# Revit family: IS_Calla_E2518_BIM_GB
name_source: partatom
category: Plumbing Fixtures
units: mm (PartAtom-declared; Revit-internal decimal feet)

## family parameters
Always vertical = No
Cut with Voids When Loaded = No
OmniClass Number = 23.45.05.21.11.11
OmniClass Title = Water Operated Water Closets
Part Type = Normal
Room Calculation Point = No
Round Connector Dimension = Use Diameter
Shared = No
Work Plane-Based = No

## types (2) — shared parameters
AreaUnits = Millimeters
BIMObjectName = IS_IdealStandard_WCseatsandcovers_Calla_E2518
BIMobject category = Wash Basins
BIMobject category code = wash-basins
BIMobject main category = Sanitary
BIMobject main category code = sanitary
BarCode = 5017830556480
Brand = Ideal Standard
Brand url = http://www.idealstandard.co.uk
Color = Gloss White
ConnectionType = Plumbing
CurrencyUnit = £
CurrentRevision = 1
Date of publishing = 15/12/2021
DurationUnit = Years
Edition number = 1
ExpectedLife = 5
Finish = Gloss White
GTIN code = https://5017830556480
Help = https://www.idealstandard.co.uk
IFC Classification = Sanitary Terminal
IfcExportAs = IfcSanitaryTerminalType
IfcExportType = WCSEAT
Installation instructions = https://www.idealstandard.co.uk
InstallationInstructions = https://www.idealstandard.co.uk
LinearUnits = Millimeter
MainColor = Gloss White
MaintenanceInformation = https://www.idealstandard.co.uk
Manufacturer = Ideal Standard
Manufacturer name = Ideal Standard
ManufacturerURL = https://www.idealstandard.co.uk
Material = MDF
Material main = MDF
NBS Reference Code = 45-35-70/391
NBS Reference Description = WC seats and covers
Name = WCseatsandcovers_Calla_E2518_IdealStandard
NettWeight = 3.4
NominalDepth = 432 mm
NominalHeight = 59 mm
NominalLength = 432 mm
NominalWidth = 363 mm
OmniClass Code = 23-31 19 00
OmniClass Description = Toilets
Product Guid = 6a91e68a-2435-4611-9eab-a73c43033e42
Product SKU = E2518
Product certification = https://www.idealstandard.co.uk
Product data url = https://bimobject.com
Product family = Calla
Product group = WC Seats
Product name = Calla Sandwich Seat & Cover Soft Closure
Product url = https://www.idealstandard.co.uk
ProductInformation = https://www.idealstandard.co.uk
QR code = http://bimobject.com
Shape = sculptured
Size = 363 x 432 x 59 mm
Space = Internal
SpareParts = https://fastpart-spares.co.uk
Technical description = https://www.idealstandard.co.uk
UNSPSC Code = 30181511
URL = https://www.idealstandard.co.uk
Uniclass 1.4 Code = L72163
Uniclass 1.4 Description = Pans, seats
Uniclass 2.0 Code = PR-31-79
Uniclass 2.0 Description = Sink, Wash Basins And Troughs
Uniclass 2015 Code = Pr_40_20_93_95
Uniclass 2015 Name = WC seats and covers
Uniclass2015Code = Pr_40_20_93_95
Uniclass2015Title = WC seats and covers
Uniclass2015Version = v1.22
Version = 1
VolumeUnits = Litres
WRASURL = https://www.wrasapprovals.co.uk
WarrantyDescription = manufacturer warranty
WarrantyDurationUnit = Years
Youtube clip = https://www.youtube.com
zero-valued in all types: DrainSize, MaterialThickness, OutletConnectionSize

## per-type parameters (varying)
| type | Description | Features | Model | ModelNumber | ModelReference |
| E2518GB - Calla Sandwich Seat & Cover SC MDF Black | Calla Sandwich Seat & Cover, Soft Close, MDF, Black | Sandwich Seat & Cover with soft close hinges in glossy black MDF | E2518GB | E2518GB | Calla Sandwich Seat & Cover SC MDF Black |
| E251801 - Calla Sandwich Seat & Cover SC MDF White | Calla Sandwich Seat & Cover, Soft Close, MDF, White | Sandwich Seat & Cover with soft close hinges in glossy white MDF | E251801 | E251801 | Calla Sandwich Seat & Cover SC MDF White |

## geometry (parser evidence)
native form markers: Sweep x3
no freeform markers — native parametric forms only
